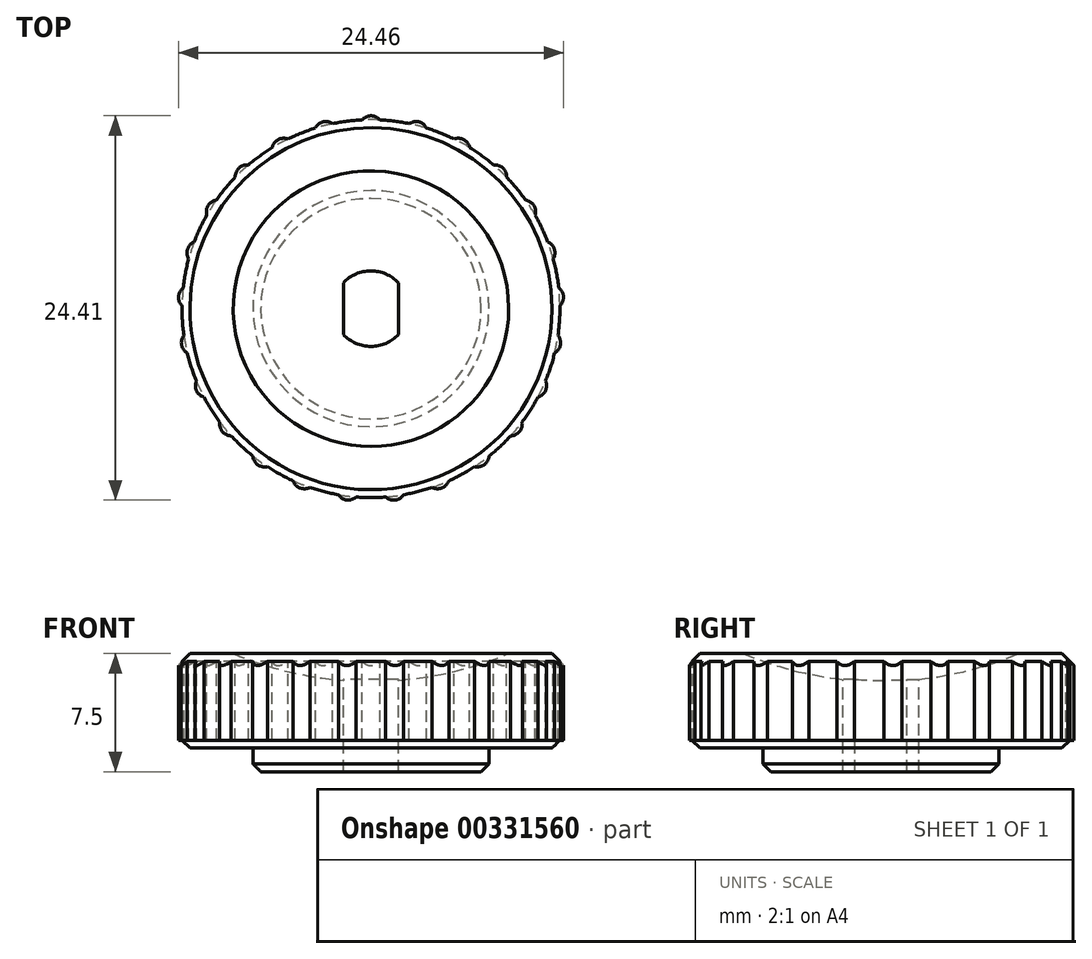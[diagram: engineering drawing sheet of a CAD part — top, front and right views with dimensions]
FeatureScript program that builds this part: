
annotation { "Feature Type Name" : "Feature", "Feature Type Description" : "" }
export const myFeature = defineFeature(function(context is Context, id is Id, definition is map)
    precondition{}
    {
        {
            var Q0;
            Q0=qCreatedBy(makeId("Top.planeOp"),FACE);
            var sketch = newSketch(context, id + "F0", { "sketchPlane" : qUnion([Q0])});
            skCircle(sketch, "E0", {"center": v(0, 0) * mm, "radius": 12 * mm});
            skLineSegment(sketch, "E1.0", {"start": v(1.75, -1.64) * mm, "end": v(1.75, 1.64) * mm});
            skLineSegment(sketch, "E2.0", {"start": v(-1.75, -1.64) * mm, "end": v(-1.75, 1.64) * mm});
            skArc(sketch, "E3", {"start": v(1.75, 1.64) * mm, "mid": v(0, 2.4) * mm, "end": v(-1.75, 1.64) * mm});
            skArc(sketch, "E4.trimOffspring", {"start": v(-1.75, -1.64) * mm, "mid": v(0, -2.4) * mm, "end": v(1.75, -1.64) * mm});
            skSolve(sketch);
        }
        {
            var Q0;
            Q0 = qSketchRegion(id + "F0", true);
            extrude(context, id + "F1", {"entities" : qUnion([Q0]), "oppositeDirection" : true, "depth" : 6 * mm});
        }
        {
            var Q0;
            Q0=qCreatedBy(makeId("Front.planeOp"),FACE);
            var sketch = newSketch(context, id + "F2", { "sketchPlane" : qUnion([Q0])});
            skLineSegment(sketch, "E5", {"start": v(0, -1.76) * mm, "end": v(0, 0) * mm});
            skLineSegment(sketch, "E6", {"start": v(-8.75, 0) * mm, "end": v(0, 0) * mm});
            skArc(sketch, "E7", {"start": v(-8.75, 0) * mm, "mid": v(-4.46, -1.32) * mm, "end": v(0, -1.76) * mm});
            skLineSegment(sketch, "E8.trimOffspring", {"start": v(0, 20.84) * mm, "end": v(0, 24.03) * mm});
            skSolve(sketch);
        }
        {
            var Q0;
            Q0 = qSketchRegion(id + "F2", true);
            var Q1;
            Q1=sQuery(id+"F2.wireOp",EDGE,"E5");
            revolve(context, id + "F3", {"operationType" : NewBodyOperationType.REMOVE, "entities" : qUnion([Q0]), "axis" : qUnion([Q1]), "revolveType" : RevolveType.FULL, "oppositeDirection" : true});
        }
        {
            var Q0;
            Q0=makeQuery(id+"F1.opExtrude","CAP_FACE",FACE,{"disambiguationData":[OSD([sQuery(id+"F0.wireOp",EDGE,"E0"),sQuery(id+"F0.wireOp",EDGE,"E1.0"),sQuery(id+"F0.wireOp",EDGE,"E2.0"),sQuery(id+"F0.wireOp",EDGE,"E3"),sQuery(id+"F0.wireOp",EDGE,"E4.trimOffspring")])],"isStart":false});
            var sketch = newSketch(context, id + "F4", { "sketchPlane" : qUnion([Q0])});
            skCircle(sketch, "E9", {"center": v(0, 0) * mm, "radius": 7.5 * mm});
            skArc(sketch, "E10.0", {"start": v(-1.75, 1.64) * mm, "mid": v(0, 2.4) * mm, "end": v(1.75, 1.64) * mm});
            skLineSegment(sketch, "E10.1", {"start": v(-1.75, 1.64) * mm, "end": v(-1.75, -1.64) * mm});
            skLineSegment(sketch, "E11.0", {"start": v(1.75, 1.64) * mm, "end": v(1.75, -1.64) * mm});
            skArc(sketch, "E12.0", {"start": v(1.75, -1.64) * mm, "mid": v(0, -2.4) * mm, "end": v(-1.75, -1.64) * mm});
            skSolve(sketch);
        }
        {
            var Q0;
            Q0 = qSketchRegion(id + "F4", true);
            extrude(context, id + "F5", {"entities" : qUnion([Q0]), "operationType" : NewBodyOperationType.ADD, "depth" : 1.5 * mm});
        }
        {
            var Q0;
            Q0=makeQuery(id+"F5.opExtrude","CAP_EDGE",EDGE,{"disambiguationData":[OSD([sQuery(id+"F4.wireOp",EDGE,"E9")])],"isStart":false});
            var Q1;
            Q1=makeQuery(id+"F1.opExtrude","CAP_EDGE",EDGE,{"disambiguationData":[OSD([sQuery(id+"F0.wireOp",EDGE,"E0")])],"isStart":false});
            chamfer(context, id + "F6", {"entities" : qUnion([Q0, Q1]), "width" : .5 * mm, "tangentPropagation" : true});
        }
        {
            var Q0;
            Q0=makeQuery(id+"F1.opExtrude","CAP_EDGE",EDGE,{"disambiguationData":[OSD([sQuery(id+"F0.wireOp",EDGE,"E0")])],"isStart":true});
            chamfer(context, id + "F7", {"entities" : qUnion([Q0]), "width" : .5 * mm, "tangentPropagation" : true});
        }
        {
            var Q0;
            Q0=makeQuery(id+"F1.opExtrude","CAP_FACE",FACE,{"disambiguationData":[OSD([sQuery(id+"F0.wireOp",EDGE,"E0"),sQuery(id+"F0.wireOp",EDGE,"E1.0"),sQuery(id+"F0.wireOp",EDGE,"E2.0"),sQuery(id+"F0.wireOp",EDGE,"E3"),sQuery(id+"F0.wireOp",EDGE,"E4.trimOffspring")])],"isStart":true});
            var sketch = newSketch(context, id + "F8", { "sketchPlane" : qUnion([Q0])});
            skCircle(sketch, "E13", {"center": v(0, 11.5) * mm, "radius": 0.75 * mm});
            skCircle(sketch, "E14.1.0", {"center": v(-2.86, 11.14) * mm, "radius": 0.75 * mm});
            skCircle(sketch, "E14.2.0", {"center": v(-5.54, 10.08) * mm, "radius": 0.75 * mm});
            skPoint(sketch, "E14.center", {"position": v(0, 0) * mm});
            skCircle(sketch, "E15.1.3.0", {"center": v(-7.87, 8.38) * mm, "radius": 0.75 * mm});
            skCircle(sketch, "E15.1.4.0", {"center": v(-9.7, 6.16) * mm, "radius": 0.75 * mm});
            skCircle(sketch, "E15.1.5.0", {"center": v(-10.94, 3.55) * mm, "radius": 0.75 * mm});
            skCircle(sketch, "E15.1.6.0", {"center": v(-11.48, 0.72) * mm, "radius": 0.75 * mm});
            skCircle(sketch, "E15.1.7.0", {"center": v(-11.3, -2.15) * mm, "radius": 0.75 * mm});
            skCircle(sketch, "E15.1.8.0", {"center": v(-10.4, -4.9) * mm, "radius": 0.75 * mm});
            skCircle(sketch, "E15.1.9.0", {"center": v(-8.86, -7.33) * mm, "radius": 0.75 * mm});
            skCircle(sketch, "E16.1.10.0", {"center": v(-6.76, -9.3) * mm, "radius": 0.75 * mm});
            skCircle(sketch, "E16.1.11.0", {"center": v(-4.23, -10.7) * mm, "radius": 0.75 * mm});
            skCircle(sketch, "E16.1.12.0", {"center": v(-1.44, -11.4) * mm, "radius": 0.75 * mm});
            skCircle(sketch, "E16.1.13.0", {"center": v(1.44, -11.4) * mm, "radius": 0.75 * mm});
            skCircle(sketch, "E16.1.14.0", {"center": v(4.23, -10.7) * mm, "radius": 0.75 * mm});
            skCircle(sketch, "E16.1.15.0", {"center": v(6.76, -9.3) * mm, "radius": 0.75 * mm});
            skCircle(sketch, "E16.1.16.0", {"center": v(8.86, -7.33) * mm, "radius": 0.75 * mm});
            skCircle(sketch, "E16.1.17.0", {"center": v(10.4, -4.9) * mm, "radius": 0.75 * mm});
            skCircle(sketch, "E16.1.18.0", {"center": v(11.3, -2.15) * mm, "radius": 0.75 * mm});
            skCircle(sketch, "E16.1.19.0", {"center": v(11.48, 0.72) * mm, "radius": 0.75 * mm});
            skCircle(sketch, "E17.1.20.0", {"center": v(10.94, 3.55) * mm, "radius": 0.75 * mm});
            skCircle(sketch, "E17.1.21.0", {"center": v(9.7, 6.16) * mm, "radius": 0.75 * mm});
            skCircle(sketch, "E17.1.22.0", {"center": v(7.87, 8.38) * mm, "radius": 0.75 * mm});
            skCircle(sketch, "E17.1.23.0", {"center": v(5.54, 10.08) * mm, "radius": 0.75 * mm});
            skCircle(sketch, "E17.1.24.0", {"center": v(2.86, 11.14) * mm, "radius": 0.75 * mm});
            skSolve(sketch);
        }
        {
            var Q0;
            Q0 = qSketchRegion(id + "F8", true);
            extrude(context, id + "F9", {"entities" : qUnion([Q0]), "operationType" : NewBodyOperationType.ADD, "oppositeDirection" : true, "depth" : 5.5 * mm});
        }
        {
            var Q0;
            Q0=qCreatedBy(makeId("Front.planeOp"),FACE);
            var sketch = newSketch(context, id + "F10", { "sketchPlane" : qUnion([Q0])});
            skLineSegment(sketch, "E18", {"start": v(17, -5.5) * mm, "end": v(6.86, 4.64) * mm});
            skLineSegment(sketch, "E19", {"start": v(0, 0) * mm, "end": v(0, -2.9) * mm});
            skLineSegment(sketch, "E20.0", {"start": v(17, 4.64) * mm, "end": v(17, -5.5) * mm});
            skLineSegment(sketch, "E21.0", {"start": v(6.86, 4.64) * mm, "end": v(17, 4.64) * mm});
            skSolve(sketch);
        }
        {
            var Q0;
            Q0 = qSketchRegion(id + "F10", true);
            var Q1;
            Q1=sQuery(id+"F10.wireOp",EDGE,"E19");
            revolve(context, id + "F11", {"operationType" : NewBodyOperationType.REMOVE, "entities" : qUnion([Q0]), "axis" : qUnion([Q1]), "revolveType" : RevolveType.FULL, "oppositeDirection" : true});
        }
    });
